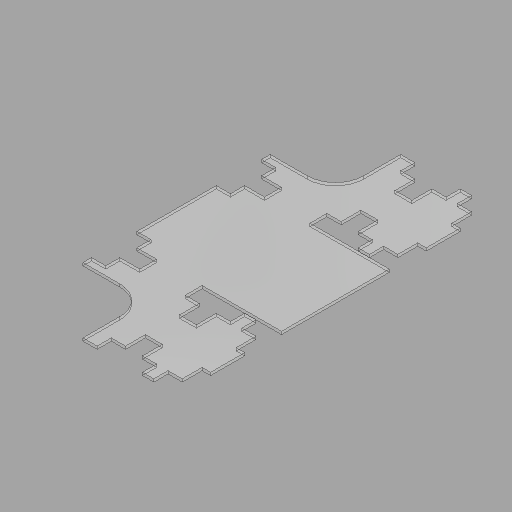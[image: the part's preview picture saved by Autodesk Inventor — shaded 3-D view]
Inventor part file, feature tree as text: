
AUTODESK INVENTOR PART (.ipt)
format: ipt  version: 2024.2 (Build 282272000, 272)  size: 825,344 bytes
history: native  units: in
note: dims shown in document units (in); Inventor stores cm internally (conversion verified against a paired STEP export)
features: extrude x9, sketch x9, projected_geometry x8
ambient origin geometry x8: Origin, YZ Plane, XZ Plane, XY Plane, X Axis, Y Axis, Z Axis, Center Point
bodies: Solid1 (feature_tree)
feature tree (26):
  extrude  "Extrusion1"  Depth=28.0in
  extrude  "Extrusion2"  Depth=3.0in
  extrude  "Extrusion3"  Depth=1.75in
  extrude  "Extrusion4"  Depth=0.25in TaperAngle=0.0deg
  extrude  "Extrusion5"  Depth=1.25in
  extrude  "Extrusion6"  Depth=1.75in
  extrude  "Extrusion7"  Depth=1.25in
  extrude  "Extrusion8"  Depth=5.75in
  extrude  "Extrusion9"  Depth=2.5in
  sketch  "Sketch1"  dims[d0=28.0in d1=28.0in]
  sketch  "Sketch2"  dims[d2=0.25in d3=0.0in d4=3.0in]
  projected_geometry  "Projected Loop1"
  sketch  "Sketch3"  dims[d5=1.25in d6=1.75in]
  projected_geometry  "Projected Loop2"
  sketch  "Sketch4"  dims[d7=1.75in d8=0.25in d9=0.0in]
  projected_geometry  "Projected Loop3"
  sketch  "Sketch5"  dims[d10=6.5in d11=1.25in]
  projected_geometry  "Projected Loop4"
  sketch  "Sketch6"  dims[d12=1.25in d13=1.75in]
  projected_geometry  "Projected Loop5"
  sketch  "Sketch7"  dims[d14=1.5in d15=1.25in]
  projected_geometry  "Projected Loop6"
  sketch  "Sketch8"  dims[d16=0.25in d17=0.0in d18=5.75in]
  projected_geometry  "Projected Loop7"
  sketch  "Sketch9"  dims[d19=5.75in d20=2.5in d21=0.25in d22=0.0in d24=6.25in d25=1.25in d26=1.25in d27=1.05in d30=1.5in d33=1.707in d34=0.846in d35=22.6875in d36=0.0in d38=6.625in d39=14.375in d40=0.0in d42=0.25in d43=0.25in d44=0.5in d45=1.25in d46=1.147in d47=1.25in d48=1.75in d49=1.5in d50=1.75in d51=1.25in d52=0.5in d53=0.5in d54=14.375in d55=0.0in d56=1.5in d57=1.0in d58=0.0in d59=0.9375in d60=0.0in d61=0.5in d62=0.0344in]
  projected_geometry  "Projected Loop8"
